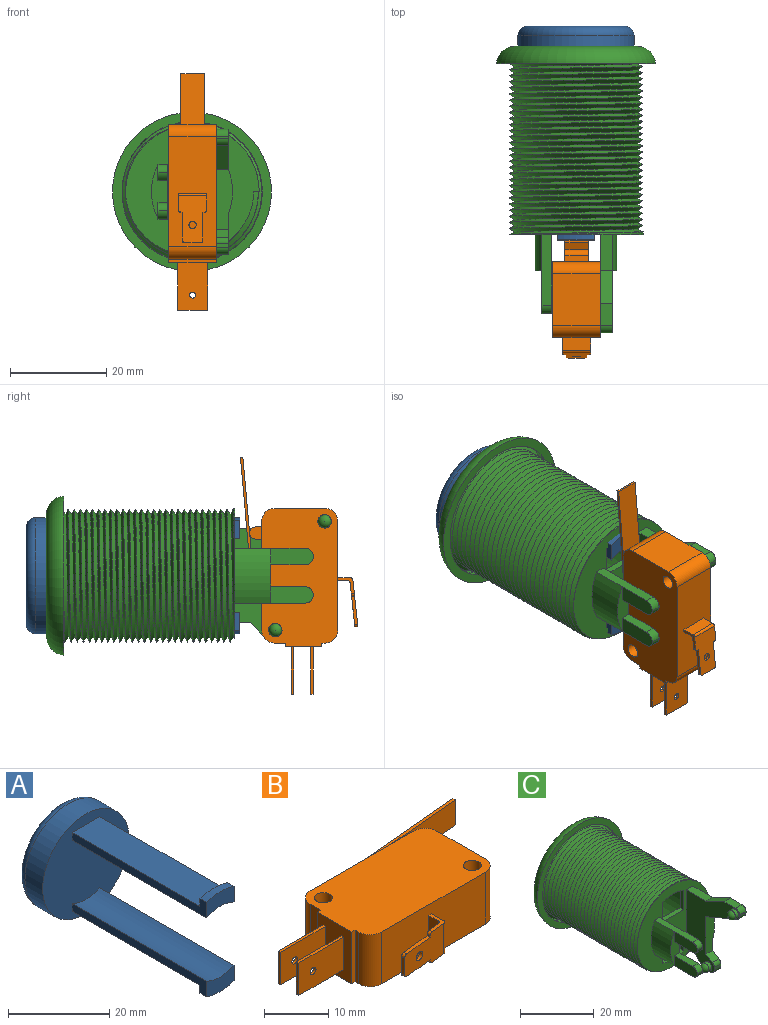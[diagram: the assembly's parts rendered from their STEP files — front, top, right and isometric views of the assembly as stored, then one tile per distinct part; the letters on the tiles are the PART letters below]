
ASSEMBLY  parts=3 mates=2
PART A: 18 faces, bbox 26.1x45.6x26.1 mm
  f0: plane 24.13x24.13mm, normal (0,-1,0), area 437.9mm2, adj f1,f5,f6,f7,f10,f11,f12,f14
  f1: cylinder r=12.06mm len=24.13mm, axis (0,-1,0), area 373.5mm2, adj f0,f3
  f2: sphere r=37.39mm, area 291.6mm2, adj f3
  f3: torus R=10.06mm, axis (0,1,0), area 255.7mm2, adj f1,f2
  f4: cylinder r=12.06mm len=7.7mm, axis (0,1,0), area 13.9mm2, adj f5,f7,f8,f17
  f5: plane 37.5x3.78mm, normal (1,0,0), area 73.4mm2, adj f0,f4,f6,f8,f16,f17
  f6: cylinder r=8.56mm len=37.5mm, axis (0,1,0), area 299.5mm2, adj f0,f5,f7,f8
  f7: plane 37.5x3.78mm, normal (-1,0,0), area 73.4mm2, adj f0,f4,f6,f8,f16,f17
  f8: plane 7.7x4.42mm, normal (0,-1,0), area 27.6mm2, adj f4,f5,f6,f7
  f9: cylinder r=12.06mm len=7.7mm, axis (0,1,0), area 13.9mm2, adj f10,f12,f13,f15
  f10: plane 37.5x3.78mm, normal (-1,0,0), area 74.4mm2, adj f0,f9,f11,f13,f14,f15
  f11: cylinder r=8.56mm len=37.5mm, axis (0,1,0), area 299.5mm2, adj f0,f10,f12,f13
  f12: plane 37.5x3.78mm, normal (1,0,0), area 74.4mm2, adj f0,f9,f11,f13,f14,f15
  f13: plane 7.7x4.42mm, normal (0,-1,0), area 27.6mm2, adj f9,f10,f11,f12
  f14: plane 35.66x7.7mm, normal (0,0,1), area 274.6mm2, adj f0,f10,f12,f15
  f15: plane 7.7x2.52mm, normal (0,1,0.03), area 17.8mm2, adj f9,f10,f12,f14
  f16: plane 35.66x7.7mm, normal (0,0,-1), area 274.6mm2, adj f0,f5,f7,f17
  f17: plane 7.7x2.55mm, normal (0,1,-0.03), area 18mm2, adj f4,f5,f7,f16
PART B: 60 faces, bbox 49.2x24.4x9.9 mm
  f0: cylinder r=0.51mm len=0.69mm, axis (-0.11,0.99,0), area 0.5mm2, adj f3,f4,f49,f56
  f1: cylinder r=0.51mm len=5.84mm, axis (0,0,-1), area 4.3mm2, adj f4,f49,f50,f52
  f2: cylinder r=0.51mm len=0.69mm, axis (0.11,-0.99,0), area 0.5mm2, adj f3,f4,f50,f53
  f3: plane 9.71x5.84mm, normal (0.11,-0.99,0), area 45.3mm2, adj f0,f2,f41,f42,f43,f48,f49,f50
  f4: plane 9.14x5.84mm, normal (-0.11,0.99,0), area 42mm2, adj f0,f1,f2,f41,f42,f48,f49,f50
  f5: plane 2.54x2.54mm, normal (0,0,1), area 5.7mm2, adj f7,f8,f9,f38
  f6: plane 2.54x2.54mm, normal (0,0,-1), area 5.7mm2, adj f7,f8,f9,f38
  f7: plane 4.83x1.27mm, normal (-1,0,0), area 6.1mm2, adj f5,f6,f8,f38
  f8: cylinder r=1.27mm len=4.83mm, axis (0,0,1), area 19.3mm2, adj f5,f6,f7,f9
  f9: plane 4.83x1.27mm, normal (1,0,0), area 6.1mm2, adj f5,f6,f8,f38
  f10: plane 27.59x4.45mm, normal (0,0,1), area 14.8mm2, adj f12,f13,f14,f15,f16,f38,f44,f45
  f11: plane 27.59x4.45mm, normal (0,0,-1), area 14.8mm2, adj f12,f13,f14,f15,f16,f38,f44,f45
  f12: plane 4.83x0.51mm, normal (1,0.09,0), area 2.5mm2, adj f10,f11,f13,f16
  f13: plane 26.62x4.83mm, normal (0.09,-1,0), area 129.1mm2, adj f10,f11,f12,f44
  f14: plane 4.83x1.06mm, normal (1,0,0), area 5.1mm2, adj f10,f11,f38,f44
  f15: plane 4.83x1.52mm, normal (-1,0,0), area 7.4mm2, adj f10,f11,f38,f45
  f16: plane 27.08x4.83mm, normal (-0.09,1,0), area 131.3mm2, adj f10,f11,f12,f45
  f17: plane 9.91x0.51mm, normal (0,0,1), area 5mm2, adj f19,f20,f21,f34
  f18: plane 9.91x0.51mm, normal (0,0,-1), area 5mm2, adj f19,f20,f21,f34
  f19: plane 9.91x6.21mm, normal (0,1,0), area 60.2mm2, adj f17,f18,f21,f34,f47
  f20: plane 9.91x6.21mm, normal (0,-1,0), area 60.2mm2, adj f17,f18,f21,f34,f47
  f21: plane 6.21x0.51mm, normal (-1,0,0), area 3.2mm2, adj f17,f18,f19,f20
  f22: plane 9.91x0.51mm, normal (0,0,1), area 5mm2, adj f24,f25,f26,f34
  f23: plane 9.91x0.51mm, normal (0,0,-1), area 5mm2, adj f24,f25,f26,f34
  f24: plane 9.91x6.21mm, normal (0,1,0), area 60.2mm2, adj f22,f23,f26,f34,f46
  f25: plane 9.91x6.21mm, normal (0,-1,0), area 60.2mm2, adj f22,f23,f26,f34,f46
  f26: plane 6.21x0.51mm, normal (-1,0,0), area 3.2mm2, adj f22,f23,f24,f25
  f27: plane 28.7x15.75mm, normal (0,0,1), area 428mm2, adj f29,f30,f31,f32,f33,f34,f35,f36
  f28: plane 28.7x15.75mm, normal (0,0,-1), area 428mm2, adj f29,f30,f31,f32,f33,f34,f35,f36
  f29: cylinder r=2.54mm len=9.91mm, axis (0,0,1), area 39.5mm2, adj f27,f28,f30,f40
  f30: plane 22.86x9.91mm, normal (0,-1,0), area 222.8mm2, adj f27,f28,f29,f31,f49,f50,f51,f52
  f31: cylinder r=2.54mm len=9.91mm, axis (0,0,1), area 39.5mm2, adj f27,f28,f30,f32
  f32: plane 9.91x0.76mm, normal (-1,0,0), area 7.6mm2, adj f27,f28,f31,f33
  f33: plane 9.91x0.76mm, normal (0,-1,0), area 7.6mm2, adj f27,f28,f32,f34
  f34: plane 9.91x7.62mm, normal (-1,0,0), area 69.2mm2, adj f17,f18,f19,f20,f22,f23,f24,f25
  f35: plane 9.91x0.76mm, normal (0,1,0), area 7.6mm2, adj f27,f28,f34,f36
  f36: plane 9.91x2.29mm, normal (-1,0,0), area 22.7mm2, adj f27,f28,f35,f37
  f37: cylinder r=2.54mm len=9.91mm, axis (0,0,1), area 39.5mm2, adj f27,f28,f36,f38
  f38: plane 22.86x9.91mm, normal (0,1,0), area 211.8mm2, adj f5,f6,f7,f9,f10,f11,f14,f15
  f39: cylinder r=2.54mm len=9.91mm, axis (0,0,1), area 39.5mm2, adj f27,f28,f38,f40
  f40: plane 10.67x9.91mm, normal (1,0,0), area 105.7mm2, adj f27,f28,f29,f39
  f41: cylinder r=0.51mm len=0.69mm, axis (0.11,-0.99,0), area 0.5mm2, adj f3,f4,f48,f55
  f42: cylinder r=0.51mm len=0.69mm, axis (0.11,-0.99,0), area 0.5mm2, adj f3,f4,f48,f54
  f43: cylinder r=0.51mm len=5.84mm, axis (0,0,1), area 4.3mm2, adj f3,f49,f50,f51
  f44: cylinder r=0.51mm len=4.83mm, axis (0,0,-1), area 3.6mm2, adj f10,f11,f13,f14
  f45: cylinder r=0.51mm len=4.83mm, axis (0,0,1), area 3.6mm2, adj f10,f11,f15,f16
  f46: cylinder r=0.64mm len=1.27mm, axis (0,1,0), area 2mm2, adj f24,f25
  f47: cylinder r=0.64mm len=1.27mm, axis (0,1,0), area 2mm2, adj f19,f20
  f48: plane 3.3x0.63mm, normal (-0.99,-0.11,0), area 2.1mm2, adj f3,f4,f41,f42
  f49: plane 3.47x3.41mm, normal (0,0,-1), area 3.7mm2, adj f0,f1,f3,f4,f30,f43,f51,f52
  f50: plane 3.47x3.41mm, normal (0,0,1), area 3.7mm2, adj f1,f2,f3,f4,f30,f43,f51,f52
  f51: plane 5.84x2.65mm, normal (1,0,0), area 15.5mm2, adj f30,f43,f49,f50
  f52: plane 5.84x2.08mm, normal (-1,0,0), area 12.2mm2, adj f1,f30,f49,f50
  f53: plane 0.63x0.25mm, normal (-0.99,-0.11,0), area 0.2mm2, adj f2,f3,f4,f54
  f54: plane 5.88x1.26mm, normal (0,0,1), area 3.7mm2, adj f3,f4,f42,f53
  f55: plane 5.88x1.26mm, normal (0,0,-1), area 3.7mm2, adj f3,f4,f41,f56
  f56: plane 0.63x0.25mm, normal (-0.99,-0.11,0), area 0.2mm2, adj f0,f3,f4,f55
  f57: cylinder r=0.76mm len=1.58mm, axis (-0.11,0.99,0), area 3mm2, adj f3,f4
  f58: cylinder r=1.4mm len=9.91mm, axis (0,0,-1), area 86.9mm2, adj f27,f28
  f59: cylinder r=1.4mm len=9.91mm, axis (0,0,-1), area 86.9mm2, adj f27,f28
PART C: 64 faces, bbox 36.6x60.3x36.6 mm
  f0: plane 20.4x8.44mm, normal (1,0,0), area 100.3mm2, adj f5,f6,f34,f36,f51,f52,f55,f58
  f1: plane 11.35x3.36mm, normal (0,-1,0), area 19.7mm2, adj f3,f31,f41,f42,f45,f46
  f2: plane 7.5x0mm, normal (1,0,0), area 0mm2, adj f32,f44
  f3: plane 16.4x8mm, normal (1,0,0), area 88.5mm2, adj f1,f5,f30,f42,f44,f49,f50
  f4: plane 26x20.4mm, normal (-1,0,0), area 217.2mm2, adj f5,f7,f34,f35,f36,f37,f39,f51
  f5: plane 28.6x27.92mm, normal (0,-1,0), area 378.4mm2, adj f0,f3,f4,f6,f14,f15,f16,f17
  f6: cylinder r=12.52mm len=9.12mm, axis (0,1,0), area 70mm2, adj f0,f5,f7,f33
  f7: plane 12.49x3.36mm, normal (0,-1,0), area 36.5mm2, adj f4,f6,f33,f53,f55
  f8: plane 33.15x33.15mm, normal (0,-1,0), area 186.5mm2, adj f10,f11,f12,f13
  f9: plane 25.42x25.42mm, normal (0,1,0), area 20.7mm2, adj f10,f20
  f10: torus R=12.71mm, axis (0,-1,0), area 542.7mm2, adj f8,f9
  f11: plane 1.86x1.77mm, normal (0.31,0,-0.95), area 1.7mm2, adj f8,f12,f13,f16,f17,f18
  f12: bspline ~29.14x29.14mm, area 73.6mm2, adj f8,f11,f13,f18
  f13: bspline ~29.33x29.33mm, area 26.7mm2, adj f8,f11,f12
  f14: plane 1.1x0.65mm, normal (0,0,-1), area 0.4mm2, adj f5,f15,f17,f19
  f15: bspline ~27.98x19.88mm, area 8.2mm2, adj f5,f14,f16,f19
  f16: bspline ~36.7x27.59mm, area 2815.8mm2, adj f5,f11,f15,f17
  f17: bspline ~36.96x27.59mm, area 3151.4mm2, adj f5,f11,f14,f16,f18
  f18: bspline ~31.31x31.31mm, area 77.3mm2, adj f11,f12,f17
  f19: cylinder r=13.97mm len=27.22mm, axis (0,1,0), area 11.2mm2, adj f5,f14,f15
  f20: cylinder r=12.45mm len=37.7mm, axis (0,1,0), area 2948.3mm2, adj f9,f21
  f21: plane 24.89x24.89mm, normal (0,1,0), area 372.9mm2, adj f20,f22,f23,f24,f25,f26,f27,f28
  f22: cylinder r=10.92mm len=8.15mm, axis (0,-1,0), area 11.8mm2, adj f5,f21,f23,f25
  f23: plane 6.45x1.41mm, normal (-1,0,0), area 9.1mm2, adj f5,f21,f22,f24
  f24: plane 8.15x1.41mm, normal (0,0,1), area 11.5mm2, adj f5,f21,f23,f25
  f25: plane 6.45x1.41mm, normal (1,0,0), area 9.1mm2, adj f5,f21,f22,f24
  f26: plane 6.45x1.41mm, normal (-1,0,0), area 9.1mm2, adj f5,f21,f27,f29
  f27: cylinder r=10.92mm len=8.15mm, axis (0,-1,0), area 11.8mm2, adj f5,f21,f26,f28
  f28: plane 6.45x1.41mm, normal (1,0,0), area 9.1mm2, adj f5,f21,f27,f29
  f29: plane 8.15x1.41mm, normal (0,0,-1), area 11.5mm2, adj f5,f21,f26,f28
  f30: plane 14.65x2mm, normal (0,0,1), area 29.3mm2, adj f3,f5,f31,f41,f49
  f31: cylinder r=12.52mm len=11.35mm, axis (0,1,0), area 88.3mm2, adj f1,f5,f30,f32
  f32: plane 7.5x2mm, normal (0,0,-1), area 15mm2, adj f2,f5,f31,f43
  f33: plane 10.75x8.44mm, normal (1,0,0), area 60.2mm2, adj f5,f6,f7,f35,f53,f54,f56,f57
  f34: plane 4.49x2.5mm, normal (0,0,1), area 11.2mm2, adj f0,f4,f52,f58
  f35: plane 2.86x2.5mm, normal (0,0,-1), area 7.2mm2, adj f4,f33,f57,f61
  f36: plane 2.5x0.43mm, normal (0,-1,0), area 1.1mm2, adj f0,f4,f58,f59
  f37: cylinder r=1.37mm len=2.73mm, axis (1,0,0), area 9.8mm2, adj f4,f63
  f38: plane 0.01x0.01mm, normal (-1,0,0), area 0mm2, adj f63
  f39: cylinder r=1.37mm len=2.73mm, axis (1,0,0), area 9.8mm2, adj f4,f62
  f40: plane 0.01x0.01mm, normal (-1,0,0), area 0mm2, adj f62
  f41: plane 8.9x3.35mm, normal (-1,0,0), area 28.5mm2, adj f1,f30,f42,f49,f50
  f42: plane 7.15x2mm, normal (0,0,-1), area 14.3mm2, adj f1,f3,f41,f50
  f43: plane 7.15x2mm, normal (0,0,-1), area 14.3mm2, adj f32,f44,f46,f48
  f44: plane 16.4x3.35mm, normal (1,0,0), area 53.6mm2, adj f2,f3,f5,f43,f45,f47,f48
  f45: plane 7.15x2mm, normal (0,0,1), area 14.3mm2, adj f1,f44,f46,f47
  f46: plane 8.9x3.35mm, normal (-1,0,0), area 28.5mm2, adj f1,f43,f45,f47,f48
  f47: cylinder r=1.75mm len=2mm, axis (-1,0,0), area 5.3mm2, adj f44,f45,f46,f48
  f48: cylinder r=1.75mm len=2mm, axis (1,0,0), area 5.3mm2, adj f43,f44,f46,f47
  f49: cylinder r=1.75mm len=2mm, axis (-1,0,0), area 5.3mm2, adj f3,f30,f41,f50
  f50: cylinder r=1.75mm len=2mm, axis (1,0,0), area 5.3mm2, adj f3,f41,f42,f49
  f51: plane 7.5x2.5mm, normal (0,0,1), area 18.8mm2, adj f0,f4,f5,f52
  f52: plane 6.91x3.25mm, normal (0,0.43,0.9), area 19.1mm2, adj f0,f4,f34,f51
  f53: plane 2.52x2.5mm, normal (0,-0.51,0.86), area 7.3mm2, adj f4,f7,f33,f60
  f54: plane 2.5x0.78mm, normal (0,-1,0), area 1.9mm2, adj f4,f33,f60,f61
  f55: plane 11.99x5.13mm, normal (0,-0.39,-0.92), area 32.6mm2, adj f0,f4,f7,f59
  f56: plane 3.33x2.5mm, normal (0,0,-1), area 8.3mm2, adj f4,f5,f33,f57
  f57: plane 3.25x3.06mm, normal (0,0.73,-0.69), area 11.2mm2, adj f4,f33,f35,f56
  f58: cylinder r=1.5mm len=2.5mm, axis (-1,0,0), area 5.9mm2, adj f0,f4,f34,f36
  f59: cylinder r=1.5mm len=2.5mm, axis (1,0,0), area 4.4mm2, adj f0,f4,f36,f55
  f60: cylinder r=1.5mm len=2.5mm, axis (1,0,0), area 3.9mm2, adj f4,f33,f53,f54
  f61: cylinder r=1.5mm len=2.5mm, axis (1,0,0), area 5.9mm2, adj f4,f33,f35,f54
  f62: torus R=0.01mm, axis (-1,0,0), area 11.7mm2, adj f39,f40
  f63: torus R=0.01mm, axis (-1,0,0), area 11.7mm2, adj f37,f38
PLACE A t=(-8.36,15.23,-12.23)mm
PLACE B rot(axis=(0,-1,0),90deg) t=(-8.24,-34.7,-12.24)mm
PLACE C t=(-8.36,14.38,-12.23)mm
MATE fastened A.f1 <-> C.f10  axis (0,-1,0) through (-8.36,15.23,-12.23)mm
MATE fastened B.f59 <-> C.f39  axis (1,0,0) through (-3.29,-39.86,-0.94)mm
